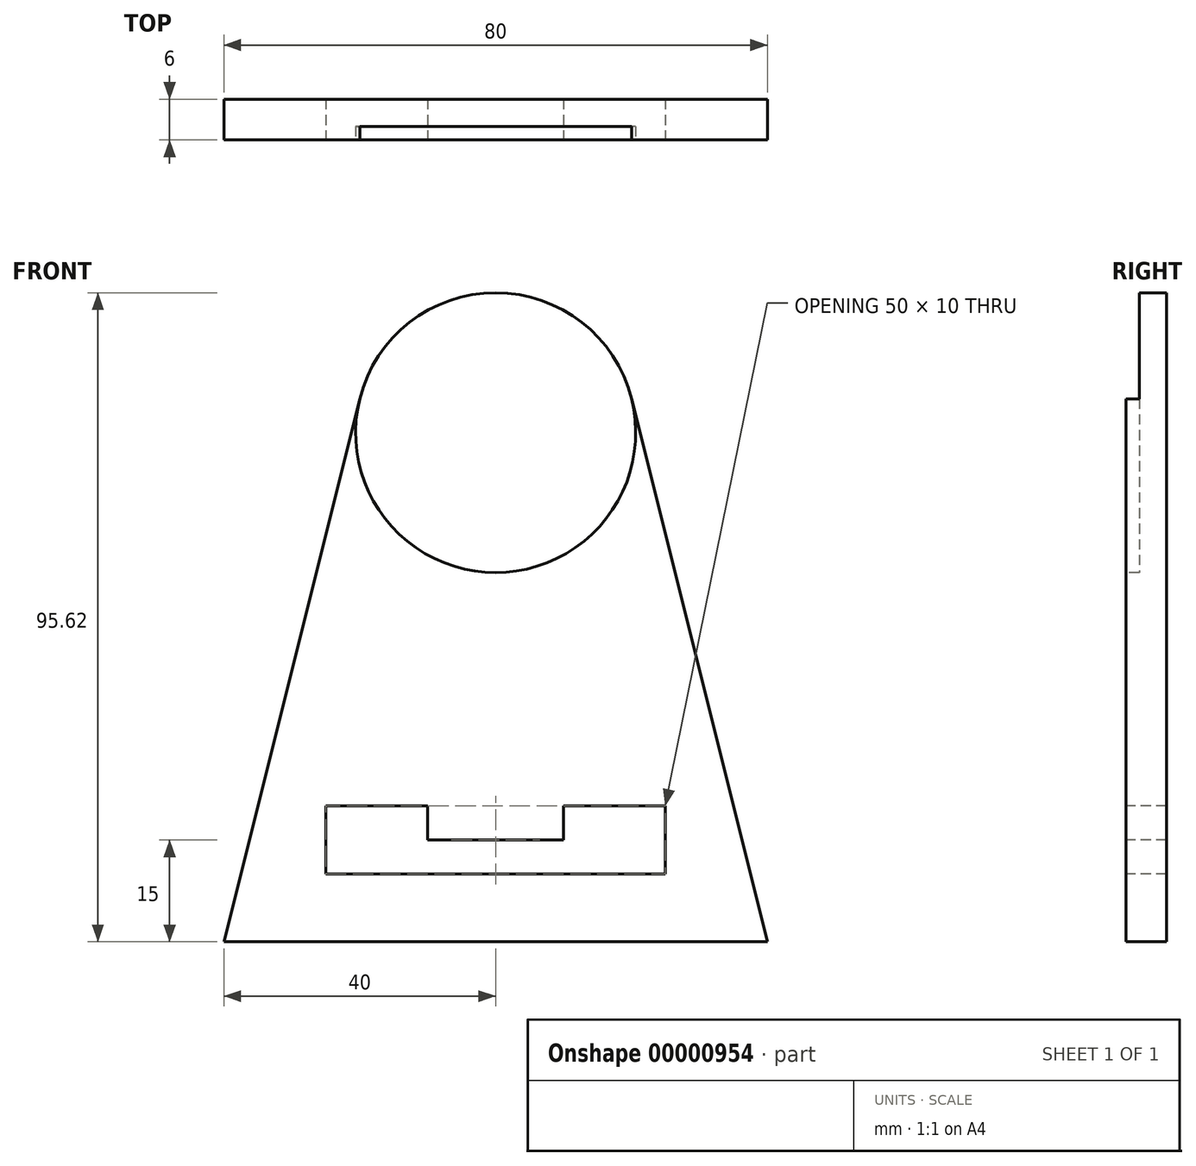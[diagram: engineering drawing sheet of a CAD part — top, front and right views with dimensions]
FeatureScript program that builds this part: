
annotation { "Feature Type Name" : "Feature", "Feature Type Description" : "" }
export const myFeature = defineFeature(function(context is Context, id is Id, definition is map)
    precondition{}
    {
        {
            var Q0;
            Q0=qCreatedBy(makeId("Front.planeOp"),FACE);
            var sketch = newSketch(context, id + "F0", { "sketchPlane" : qUnion([Q0])});
            skLineSegment(sketch, "E0", {"start": v(0, 0) * mm, "end": v(80, 0) * mm});
            skLineSegment(sketch, "E1", {"start": v(80, 0) * mm, "end": v(60, 80) * mm});
            skLineSegment(sketch, "E2", {"start": v(0, 0) * mm, "end": v(20, 80) * mm});
            skLineSegment(sketch, "E3", {"start": v(20, 80) * mm, "end": v(60, 80) * mm, "construction": true});
            skArc(sketch, "E4", {"start": v(60, 80) * mm, "mid": v(40, 95.62) * mm, "end": v(20, 80) * mm});
            skLineSegment(sketch, "E5", {"start": v(40, 80) * mm, "end": v(40, 0) * mm, "construction": true});
            skSolve(sketch);
        }
        {
            var Q0;
            Q0=makeQuery(id+"F0.imprint","IMPRINT",FACE,{"disambiguationData":[TD([[makeQuery(id+"F0.imprint","IMPRINT",EDGE,{"derivedFrom":sQuery(id+"F0.wireOp",EDGE,"E0")}),1.0]])]});
            extrude(context, id + "F1", {"entities" : qUnion([Q0]), "depth" : 6 * mm});
        }
        {
            var Q0;
            Q0=makeQuery(id+"F1.opExtrude","CAP_FACE",FACE,{"disambiguationData":[OSD([sQuery(id+"F0.wireOp",EDGE,"E0"),sQuery(id+"F0.wireOp",EDGE,"E1"),sQuery(id+"F0.wireOp",EDGE,"E2"),sQuery(id+"F0.wireOp",EDGE,"E4")])],"isStart":false});
            var sketch = newSketch(context, id + "F2", { "sketchPlane" : qUnion([Q0])});
            skCircle(sketch, "E6", {"center": v(40, 75) * mm, "radius": 20.62 * mm});
            skSolve(sketch);
        }
        {
            var Q0;
            {var subQ0=sQuery(id+"F2.wireOp",EDGE,"E6");var subQ2=makeQuery(id+"F2.imprint","INTERSECT",VERTEX,{"derivedFrom":[makeQuery(id+"F1.opExtrude","CAP_EDGE",EDGE,{"disambiguationData":[OSD([sQuery(id+"F0.wireOp",EDGE,"E1")])],"isStart":false}),subQ0]});Q0=makeQuery(id+"F2.imprint","IMPRINT",FACE,{"disambiguationData":[TD([[makeQuery(id+"F2.imprint","IMPRINT",EDGE,{"disambiguationData":[TD([[subQ2,-1.0]])],"derivedFrom":subQ0}),1.0]])]});}
            extrude(context, id + "F3", {"entities" : qUnion([Q0]), "operationType" : NewBodyOperationType.REMOVE, "oppositeDirection" : true, "depth" : 2 * mm});
        }
        {
            var Q0;
            Q0=makeQuery(id+"F1.opExtrude","CAP_FACE",FACE,{"disambiguationData":[OSD([sQuery(id+"F0.wireOp",EDGE,"E0"),sQuery(id+"F0.wireOp",EDGE,"E1"),sQuery(id+"F0.wireOp",EDGE,"E2"),sQuery(id+"F0.wireOp",EDGE,"E4")])],"isStart":false});
            var sketch = newSketch(context, id + "F4", { "sketchPlane" : qUnion([Q0])});
            skLineSegment(sketch, "E7", {"start": v(15, 20) * mm, "end": v(15, 10) * mm});
            skLineSegment(sketch, "E8", {"start": v(15, 10) * mm, "end": v(65, 10) * mm});
            skLineSegment(sketch, "E9", {"start": v(65, 10) * mm, "end": v(65, 20) * mm});
            skLineSegment(sketch, "E10", {"start": v(65, 20) * mm, "end": v(50, 20) * mm});
            skLineSegment(sketch, "E11", {"start": v(30, 15) * mm, "end": v(30, 20) * mm});
            skLineSegment(sketch, "E12", {"start": v(15, 20) * mm, "end": v(30, 20) * mm});
            skLineSegment(sketch, "E13", {"start": v(30, 15) * mm, "end": v(50, 15) * mm});
            skLineSegment(sketch, "E14", {"start": v(50, 15) * mm, "end": v(50, 20) * mm});
            skLineSegment(sketch, "E15", {"start": v(40, 0) * mm, "end": v(40, 10) * mm, "construction": true});
            skSolve(sketch);
        }
        {
            var Q0;
            Q0 = qSketchRegion(id + "F4", true);
            extrude(context, id + "F5", {"entities" : qUnion([Q0]), "operationType" : NewBodyOperationType.REMOVE, "oppositeDirection" : true, "depth" : 25 * mm});
        }
    });
